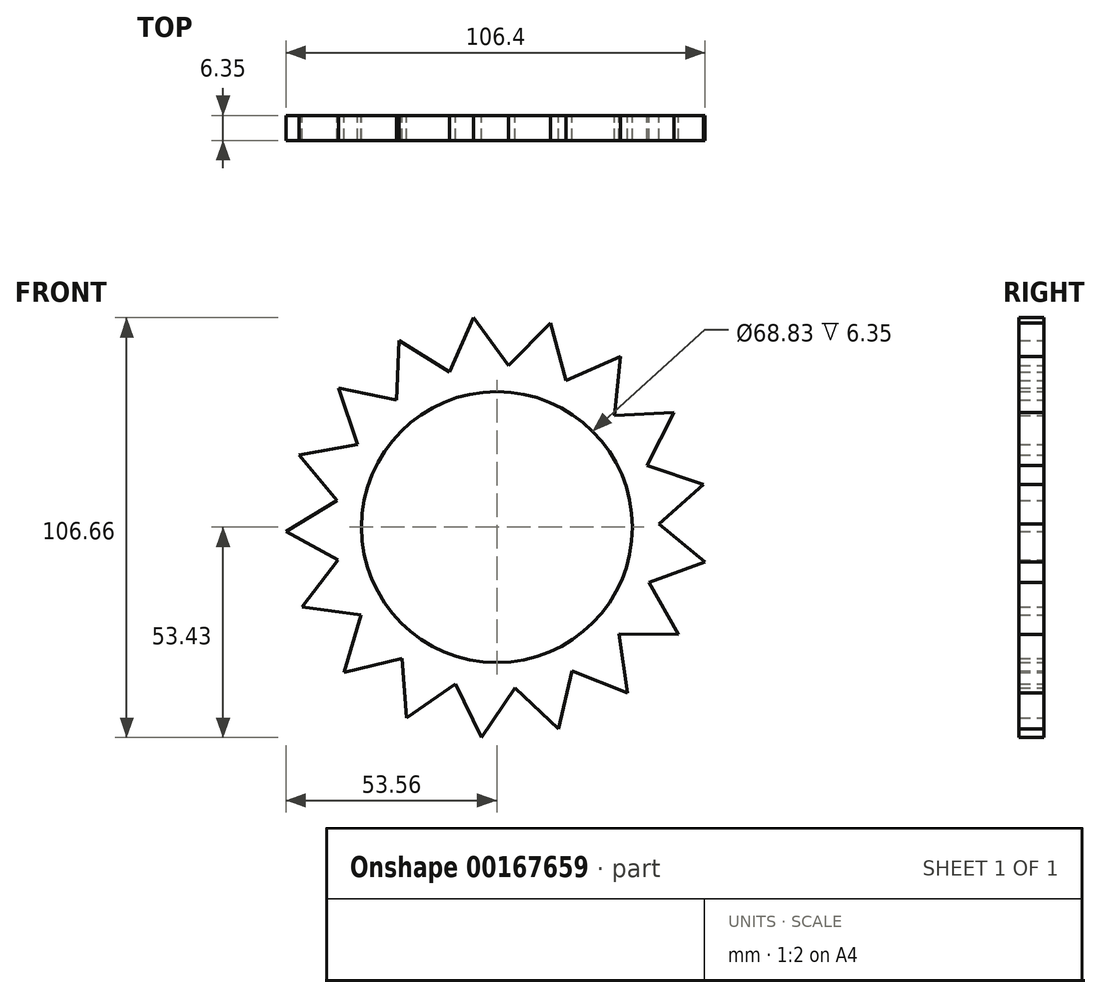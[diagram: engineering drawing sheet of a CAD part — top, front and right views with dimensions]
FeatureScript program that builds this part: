
annotation { "Feature Type Name" : "Feature", "Feature Type Description" : "" }
export const myFeature = defineFeature(function(context is Context, id is Id, definition is map)
    precondition{}
    {
        {
            var Q0;
            Q0=qCreatedBy(makeId("Front.planeOp"),FACE);
            var sketch = newSketch(context, id + "F0", { "sketchPlane" : qUnion([Q0])});
            skCircle(sketch, "E0", {"center": v(0, 0) * mm, "radius": 34.42 * mm});
            skLineSegment(sketch, "E1.0", {"start": v(-15.38, 30.35) * mm, "end": v(-32.13, 11.25) * mm});
            skLineSegment(sketch, "E1.1", {"start": v(-32.13, 11.25) * mm, "end": v(-40.3, 35.3) * mm});
            skLineSegment(sketch, "E1.2", {"start": v(-40.3, 35.3) * mm, "end": v(-15.38, 30.35) * mm});
            skPoint(sketch, "E1.0.midPoint", {"position": v(-23.76, 20.8) * mm});
            skLineSegment(sketch, "E2.1.0", {"start": v(-34.02, -1.12) * mm, "end": v(-50.33, 18.36) * mm});
            skLineSegment(sketch, "E2.1.1", {"start": v(-50.33, 18.36) * mm, "end": v(-25.3, 22.74) * mm});
            skLineSegment(sketch, "E2.1.2", {"start": v(-25.3, 22.74) * mm, "end": v(-34.02, -1.12) * mm});
            skLineSegment(sketch, "E2.2.0", {"start": v(-31.32, -13.33) * mm, "end": v(-53.56, -1.06) * mm});
            skLineSegment(sketch, "E2.2.1", {"start": v(-53.56, -1.06) * mm, "end": v(-31.81, 12.06) * mm});
            skLineSegment(sketch, "E2.2.2", {"start": v(-31.81, 12.06) * mm, "end": v(-31.32, -13.33) * mm});
            skLineSegment(sketch, "E2.3.0", {"start": v(-24.39, -23.75) * mm, "end": v(-49.56, -20.34) * mm});
            skLineSegment(sketch, "E2.3.1", {"start": v(-49.56, -20.34) * mm, "end": v(-34.02, -0.24) * mm});
            skLineSegment(sketch, "E2.3.2", {"start": v(-34.02, -0.24) * mm, "end": v(-24.39, -23.75) * mm});
            skLineSegment(sketch, "E2.4.0", {"start": v(-14.16, -30.95) * mm, "end": v(-38.87, -36.87) * mm});
            skLineSegment(sketch, "E2.4.1", {"start": v(-38.87, -36.87) * mm, "end": v(-31.64, -12.52) * mm});
            skLineSegment(sketch, "E2.4.2", {"start": v(-31.64, -12.52) * mm, "end": v(-14.16, -30.95) * mm});
            skLineSegment(sketch, "E2.5.0", {"start": v(-2.03, -33.98) * mm, "end": v(-22.92, -48.42) * mm});
            skLineSegment(sketch, "E2.5.1", {"start": v(-22.92, -48.42) * mm, "end": v(-24.98, -23.1) * mm});
            skLineSegment(sketch, "E2.5.2", {"start": v(-24.98, -23.1) * mm, "end": v(-2.03, -33.98) * mm});
            skLineSegment(sketch, "E2.6.0", {"start": v(10.39, -32.42) * mm, "end": v(-3.88, -53.43) * mm});
            skLineSegment(sketch, "E2.6.1", {"start": v(-3.88, -53.43) * mm, "end": v(-14.95, -30.56) * mm});
            skLineSegment(sketch, "E2.6.2", {"start": v(-14.95, -30.56) * mm, "end": v(10.39, -32.42) * mm});
            skLineSegment(sketch, "E2.7.0", {"start": v(21.4, -26.48) * mm, "end": v(15.68, -51.22) * mm});
            skLineSegment(sketch, "E2.7.1", {"start": v(15.68, -51.22) * mm, "end": v(-2.9, -33.9) * mm});
            skLineSegment(sketch, "E2.7.2", {"start": v(-2.9, -33.9) * mm, "end": v(21.4, -26.48) * mm});
            skLineSegment(sketch, "E3", {"start": v(34.42, 0) * mm, "end": v(-34.42, 0) * mm});
            skLineSegment(sketch, "E4.1.8.0", {"start": v(29.51, -16.96) * mm, "end": v(33.12, -42.1) * mm});
            skLineSegment(sketch, "E4.3.8.0", {"start": v(33.12, -42.1) * mm, "end": v(9.55, -32.66) * mm});
            skLineSegment(sketch, "E4.6.8.0", {"start": v(9.55, -32.66) * mm, "end": v(29.51, -16.96) * mm});
            skLineSegment(sketch, "E4.1.9.0", {"start": v(33.65, -5.15) * mm, "end": v(46.1, -27.3) * mm});
            skLineSegment(sketch, "E4.3.9.0", {"start": v(46.1, -27.3) * mm, "end": v(20.7, -27) * mm});
            skLineSegment(sketch, "E4.6.9.0", {"start": v(20.7, -27) * mm, "end": v(33.65, -5.15) * mm});
            skLineSegment(sketch, "E5.1.10.0", {"start": v(33.24, 7.35) * mm, "end": v(52.84, -8.8) * mm});
            skLineSegment(sketch, "E5.3.10.0", {"start": v(52.84, -8.8) * mm, "end": v(29.05, -17.7) * mm});
            skLineSegment(sketch, "E5.6.10.0", {"start": v(29.05, -17.7) * mm, "end": v(33.24, 7.35) * mm});
            skLineSegment(sketch, "E5.1.11.0", {"start": v(28.34, 18.86) * mm, "end": v(52.45, 10.89) * mm});
            skLineSegment(sketch, "E5.3.11.0", {"start": v(52.45, 10.89) * mm, "end": v(33.49, -6.01) * mm});
            skLineSegment(sketch, "E5.6.11.0", {"start": v(33.49, -6.01) * mm, "end": v(28.34, 18.86) * mm});
            skLineSegment(sketch, "E5.1.12.0", {"start": v(19.61, 27.82) * mm, "end": v(44.98, 29.1) * mm});
            skLineSegment(sketch, "E5.3.12.0", {"start": v(44.98, 29.1) * mm, "end": v(33.4, 6.5) * mm});
            skLineSegment(sketch, "E5.6.12.0", {"start": v(33.4, 6.5) * mm, "end": v(19.61, 27.82) * mm});
            skLineSegment(sketch, "E5.1.13.0", {"start": v(8.23, 33.03) * mm, "end": v(31.43, 43.38) * mm});
            skLineSegment(sketch, "E5.3.13.0", {"start": v(31.43, 43.38) * mm, "end": v(28.8, 18.12) * mm});
            skLineSegment(sketch, "E5.6.13.0", {"start": v(28.8, 18.12) * mm, "end": v(8.23, 33.03) * mm});
            skLineSegment(sketch, "E5.1.14.0", {"start": v(-4.25, 33.77) * mm, "end": v(13.64, 51.8) * mm});
            skLineSegment(sketch, "E5.3.14.0", {"start": v(13.64, 51.8) * mm, "end": v(20.3, 27.3) * mm});
            skLineSegment(sketch, "E5.6.14.0", {"start": v(20.3, 27.3) * mm, "end": v(-4.25, 33.77) * mm});
            skLineSegment(sketch, "E5.1.15.0", {"start": v(-16.17, 29.96) * mm, "end": v(-6, 53.23) * mm});
            skLineSegment(sketch, "E5.3.15.0", {"start": v(-6, 53.23) * mm, "end": v(9.08, 32.8) * mm});
            skLineSegment(sketch, "E5.6.15.0", {"start": v(9.08, 32.8) * mm, "end": v(-16.17, 29.96) * mm});
            skLineSegment(sketch, "E6.1.16.0", {"start": v(-25.9, 22.1) * mm, "end": v(-24.82, 47.47) * mm});
            skLineSegment(sketch, "E6.3.16.0", {"start": v(-24.82, 47.47) * mm, "end": v(-3.38, 33.85) * mm});
            skLineSegment(sketch, "E6.6.16.0", {"start": v(-3.38, 33.85) * mm, "end": v(-25.9, 22.1) * mm});
            skSolve(sketch);
        }
        {
            var Q0;
            Q0 = qSketchRegion(id + "F0", true);
            extrude(context, id + "F1", {"entities" : qUnion([Q0]), "depth" : 6.35 * mm});
        }
    });
